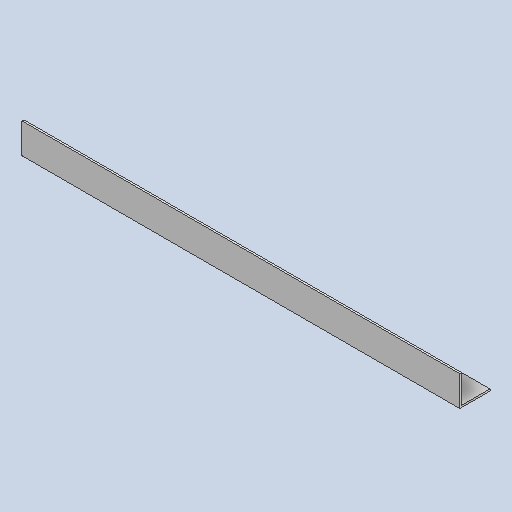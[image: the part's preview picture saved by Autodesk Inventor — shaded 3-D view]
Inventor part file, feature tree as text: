
AUTODESK INVENTOR PART (.ipt)
format: ipt  version: 2023 (Build 270158030, 158C)  size: 83,968 bytes
history: native  units: in
note: dims shown in document units (in); Inventor stores cm internally (conversion verified against a paired STEP export)
features: extrude x1, sketch x1
ambient origin geometry x8: Origin, YZ Plane, XZ Plane, XY Plane, X Axis, Y Axis, Z Axis, Center Point
bodies: Solid1 (feature_tree)
feature tree (2):
  extrude  "Extrusion1"  Depth=0.125in
  sketch  "Sketch1"  dims[d0=2.0in d1=0.125in d2=1.875in d3=1.875in d4=29.0in d5=0.0in]
